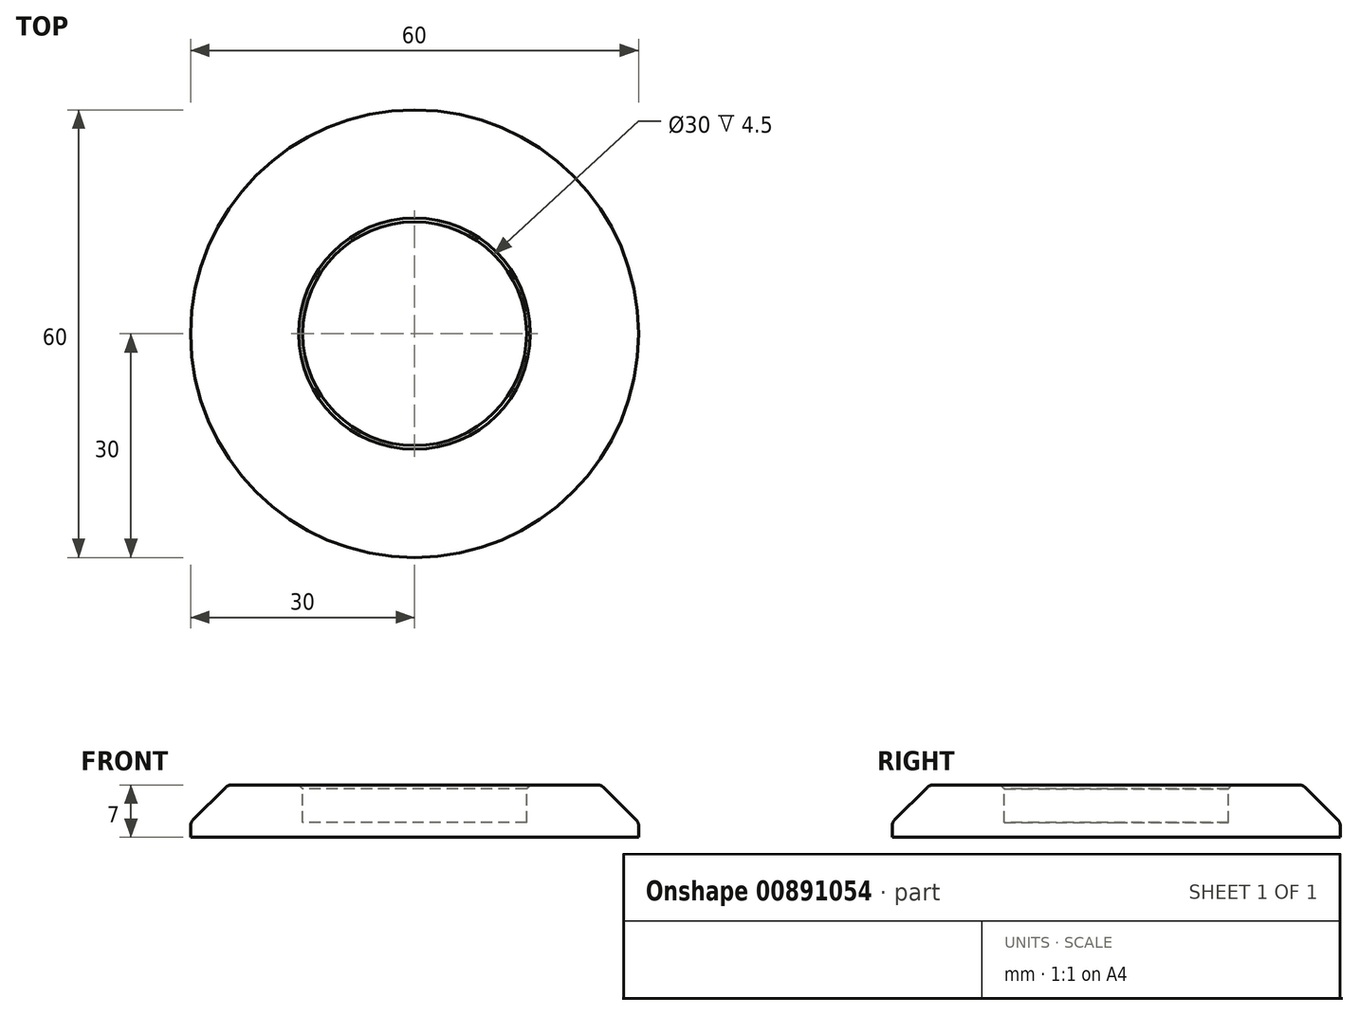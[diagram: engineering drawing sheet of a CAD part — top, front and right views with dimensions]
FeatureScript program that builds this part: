
annotation { "Feature Type Name" : "Feature", "Feature Type Description" : "" }
export const myFeature = defineFeature(function(context is Context, id is Id, definition is map)
    precondition{}
    {
        {
            var Q0;
            Q0=qCreatedBy(makeId("Front.planeOp"),FACE);
            var sketch = newSketch(context, id + "F0", { "sketchPlane" : qUnion([Q0])});
            skLineSegment(sketch, "E0", {"start": v(0, 22.68) * mm, "end": v(0, 10.85) * mm, "construction": true});
            skLineSegment(sketch, "E1", {"start": v(0, 2) * mm, "end": v(15, 2) * mm});
            skLineSegment(sketch, "E2", {"start": v(15, 2) * mm, "end": v(15, 7) * mm});
            skLineSegment(sketch, "E3", {"start": v(15, 7) * mm, "end": v(30, 7) * mm});
            skLineSegment(sketch, "E4", {"start": v(30, 7) * mm, "end": v(30, 0) * mm});
            skLineSegment(sketch, "E5", {"start": v(30, 0) * mm, "end": v(0, 0) * mm});
            skLineSegment(sketch, "E6", {"start": v(0, 0) * mm, "end": v(0, 2) * mm});
            skSolve(sketch);
        }
        {
            var Q0;
            Q0 = qSketchRegion(id + "F0", true);
            var Q1;
            Q1=sQuery(id+"F0.wireOp",EDGE,"E0");
            revolve(context, id + "F1", {"surfaceOperationType" : NewSurfaceOperationType.NEW, "entities" : qUnion([Q0]), "axis" : qUnion([Q1]), "revolveType" : RevolveType.FULL});
        }
        {
            var Q0;
            Q0=makeQuery(id+"F1.opRevolve","SWEPT_EDGE",EDGE,{"disambiguationData":[OSD([sQuery(id+"F0.wireOp",EDGE,"E3"),sQuery(id+"F0.wireOp",EDGE,"E4")])]});
            chamfer(context, id + "F2", {"entities" : qUnion([Q0]), "width" : 5 * mm, "tangentPropagation" : true});
        }
        {
            var Q0;
            Q0=makeQuery(id+"F1.opRevolve","SWEPT_EDGE",EDGE,{"disambiguationData":[OSD([sQuery(id+"F0.wireOp",EDGE,"E2"),sQuery(id+"F0.wireOp",EDGE,"E3")])]});
            chamfer(context, id + "F3", {"entities" : qUnion([Q0]), "width" : 0.5 * mm, "tangentPropagation" : true});
        }
        {
            var Q0;
            {var subQ0=sQuery(id+"F0.wireOp",EDGE,"E3");Q0=makeQuery(id+"F2.opChamfer","BLEND_EDGE",EDGE,{"blendedFrom":[makeQuery(id+"F1.opRevolve","SWEPT_EDGE",EDGE,{"disambiguationData":[OSD([subQ0,sQuery(id+"F0.wireOp",EDGE,"E4")])]}),makeQuery(id+"F1.opRevolve","SWEPT_FACE",FACE,{"disambiguationData":[OSD([subQ0])]})],"blendedInto":[makeQuery(id+"F1.opRevolve","SWEPT_FACE",FACE,{"disambiguationData":[OSD([subQ0])]})]});}
            var Q1;
            {var subQ0=sQuery(id+"F0.wireOp",EDGE,"E4");Q1=makeQuery(id+"F2.opChamfer","BLEND_EDGE",EDGE,{"blendedFrom":[makeQuery(id+"F1.opRevolve","SWEPT_EDGE",EDGE,{"disambiguationData":[OSD([sQuery(id+"F0.wireOp",EDGE,"E3"),subQ0])]}),makeQuery(id+"F1.opRevolve","SWEPT_FACE",FACE,{"disambiguationData":[OSD([subQ0])]})],"blendedInto":[makeQuery(id+"F1.opRevolve","SWEPT_FACE",FACE,{"disambiguationData":[OSD([subQ0])]})]});}
            fillet(context, id + "F4", {"entities" : qUnion([Q0, Q1]), "radius" : 1 * mm, "tangentPropagation" : true, "allowEdgeOverflow" : false});
        }
    });
